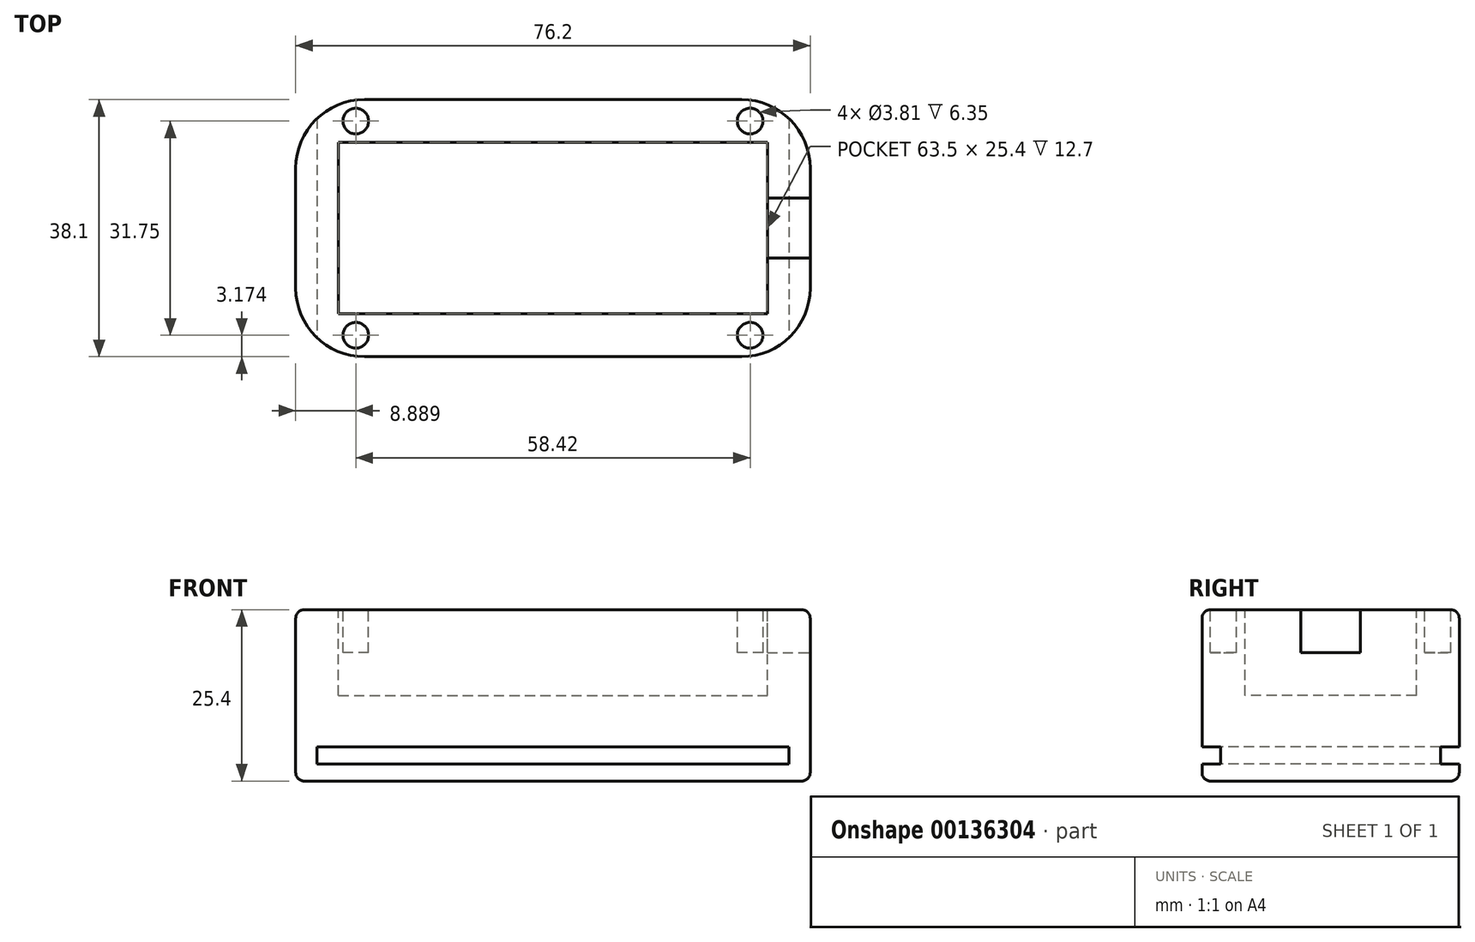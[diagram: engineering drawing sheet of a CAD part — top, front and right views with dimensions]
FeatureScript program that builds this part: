
annotation { "Feature Type Name" : "Feature", "Feature Type Description" : "" }
export const myFeature = defineFeature(function(context is Context, id is Id, definition is map)
    precondition{}
    {
        {
            var Q0;
            Q0=qCreatedBy(makeId("Top.planeOp"),FACE);
            var sketch = newSketch(context, id + "F0", { "sketchPlane" : qUnion([Q0])});
            skLineSegment(sketch, "E0.bottom", {"start": v(-49.17, 10.49) * mm, "end": v(27.03, 10.49) * mm});
            skLineSegment(sketch, "E0.top", {"start": v(-49.17, -27.61) * mm, "end": v(27.03, -27.61) * mm});
            skLineSegment(sketch, "E0.left", {"start": v(-49.17, 10.49) * mm, "end": v(-49.17, -27.61) * mm});
            skLineSegment(sketch, "E0.right", {"start": v(27.03, 10.49) * mm, "end": v(27.03, -27.61) * mm});
            skSolve(sketch);
        }
        {
            var Q0;
            Q0=makeQuery(id+"F0.imprint","IMPRINT",FACE,{"disambiguationData":[TD([[makeQuery(id+"F0.imprint","IMPRINT",EDGE,{"derivedFrom":sQuery(id+"F0.wireOp",EDGE,"E0.bottom")}),-1.0]])]});
            extrude(context, id + "F1", {"entities" : qUnion([Q0]), "depth" : 25.4 * mm});
        }
        {
            var Q0;
            Q0=makeQuery(id+"F1.opExtrude","SWEPT_FACE",FACE,{"disambiguationData":[OSD([sQuery(id+"F0.wireOp",EDGE,"E0.top")])]});
            var sketch = newSketch(context, id + "F2", { "sketchPlane" : qUnion([Q0])});
            skLineSegment(sketch, "E1.bottom", {"start": v(-46, 5.08) * mm, "end": v(23.85, 5.08) * mm});
            skLineSegment(sketch, "E1.top", {"start": v(-46, 2.54) * mm, "end": v(23.85, 2.54) * mm});
            skLineSegment(sketch, "E1.left", {"start": v(-46, 5.08) * mm, "end": v(-46, 2.54) * mm});
            skLineSegment(sketch, "E1.right", {"start": v(23.85, 5.08) * mm, "end": v(23.85, 2.54) * mm});
            skSolve(sketch);
        }
        {
            var Q0;
            Q0=makeQuery(id+"F2.imprint","IMPRINT",FACE,{"disambiguationData":[TD([[makeQuery(id+"F2.imprint","IMPRINT",EDGE,{"derivedFrom":sQuery(id+"F2.wireOp",EDGE,"E1.bottom")}),-1.0]])]});
            extrude(context, id + "F3", {"entities" : qUnion([Q0]), "operationType" : NewBodyOperationType.REMOVE, "endBound" : BoundingType.THROUGH_ALL, "oppositeDirection" : true, "depth" : 25.4 * mm});
        }
        {
            var Q0;
            Q0=makeQuery(id+"F1.opExtrude","CAP_FACE",FACE,{"disambiguationData":[OSD([sQuery(id+"F0.wireOp",EDGE,"E0.bottom"),sQuery(id+"F0.wireOp",EDGE,"E0.top"),sQuery(id+"F0.wireOp",EDGE,"E0.left"),sQuery(id+"F0.wireOp",EDGE,"E0.right")])],"isStart":false});
            var sketch = newSketch(context, id + "F4", { "sketchPlane" : qUnion([Q0])});
            skLineSegment(sketch, "E2.bottom", {"start": v(-42.82, 4.14) * mm, "end": v(20.68, 4.14) * mm});
            skLineSegment(sketch, "E2.top", {"start": v(-42.82, -21.26) * mm, "end": v(20.68, -21.26) * mm});
            skLineSegment(sketch, "E2.left", {"start": v(-42.82, 4.14) * mm, "end": v(-42.82, -21.26) * mm});
            skLineSegment(sketch, "E2.right", {"start": v(20.68, 4.14) * mm, "end": v(20.68, -21.26) * mm});
            skSolve(sketch);
        }
        {
            var Q0;
            Q0=makeQuery(id+"F4.imprint","IMPRINT",FACE,{"disambiguationData":[TD([[makeQuery(id+"F4.imprint","IMPRINT",EDGE,{"derivedFrom":sQuery(id+"F4.wireOp",EDGE,"E2.bottom")}),-1.0]])]});
            var Q1;
            Q1 = qSketchRegion(id + "F4", true);
            extrude(context, id + "F5", {"entities" : qUnion([Q0, Q1]), "operationType" : NewBodyOperationType.REMOVE, "oppositeDirection" : true, "depth" : 12.7 * mm});
        }
        {
            var Q0;
            Q0=makeQuery(id+"F1.opExtrude","CAP_FACE",FACE,{"disambiguationData":[OSD([sQuery(id+"F0.wireOp",EDGE,"E0.bottom"),sQuery(id+"F0.wireOp",EDGE,"E0.top"),sQuery(id+"F0.wireOp",EDGE,"E0.left"),sQuery(id+"F0.wireOp",EDGE,"E0.right")])],"isStart":false});
            var sketch = newSketch(context, id + "F6", { "sketchPlane" : qUnion([Q0])});
            skLineSegment(sketch, "E3.bottom", {"start": v(20.68, -4.12) * mm, "end": v(27.03, -4.12) * mm});
            skLineSegment(sketch, "E3.top", {"start": v(20.68, -13) * mm, "end": v(27.03, -13) * mm});
            skLineSegment(sketch, "E3.left", {"start": v(20.68, -4.12) * mm, "end": v(20.68, -13) * mm});
            skLineSegment(sketch, "E3.right", {"start": v(27.03, -4.12) * mm, "end": v(27.03, -13) * mm});
            skSolve(sketch);
        }
        {
            var Q0;
            Q0=makeQuery(id+"F6.imprint","IMPRINT",FACE,{"disambiguationData":[TD([[makeQuery(id+"F6.imprint","IMPRINT",EDGE,{"derivedFrom":sQuery(id+"F6.wireOp",EDGE,"E3.bottom")}),-1.0]])]});
            extrude(context, id + "F7", {"entities" : qUnion([Q0]), "operationType" : NewBodyOperationType.REMOVE, "oppositeDirection" : true, "depth" : 6.35 * mm});
        }
        {
            var Q0;
            Q0=makeQuery(id+"F1.opExtrude","CAP_FACE",FACE,{"disambiguationData":[OSD([sQuery(id+"F0.wireOp",EDGE,"E0.bottom"),sQuery(id+"F0.wireOp",EDGE,"E0.top"),sQuery(id+"F0.wireOp",EDGE,"E0.left"),sQuery(id+"F0.wireOp",EDGE,"E0.right")])],"isStart":false});
            var sketch = newSketch(context, id + "F8", { "sketchPlane" : qUnion([Q0])});
            skCircle(sketch, "E4", {"center": v(-40.28, 7.31) * mm, "radius": 1.9 * mm});
            skCircle(sketch, "E5", {"center": v(18.14, 7.31) * mm, "radius": 1.9 * mm});
            skCircle(sketch, "E6", {"center": v(-40.28, -24.44) * mm, "radius": 1.9 * mm});
            skCircle(sketch, "E7", {"center": v(18.14, -24.44) * mm, "radius": 1.9 * mm});
            skSolve(sketch);
        }
        {
            var Q0;
            Q0 = qSketchRegion(id + "F8", true);
            extrude(context, id + "F9", {"entities" : qUnion([Q0]), "operationType" : NewBodyOperationType.REMOVE, "oppositeDirection" : true, "depth" : 6.35 * mm});
        }
        {
            var Q0;
            Q0=makeQuery(id+"F1.opExtrude","SWEPT_EDGE",EDGE,{"disambiguationData":[OSD([sQuery(id+"F0.wireOp",EDGE,"E0.top"),sQuery(id+"F0.wireOp",EDGE,"E0.left")])]});
            var Q1;
            Q1=makeQuery(id+"F1.opExtrude","SWEPT_EDGE",EDGE,{"disambiguationData":[OSD([sQuery(id+"F0.wireOp",EDGE,"E0.top"),sQuery(id+"F0.wireOp",EDGE,"E0.right")])]});
            var Q2;
            Q2=makeQuery(id+"F1.opExtrude","SWEPT_EDGE",EDGE,{"disambiguationData":[OSD([sQuery(id+"F0.wireOp",EDGE,"E0.bottom"),sQuery(id+"F0.wireOp",EDGE,"E0.right")])]});
            var Q3;
            Q3=makeQuery(id+"F1.opExtrude","SWEPT_EDGE",EDGE,{"disambiguationData":[OSD([sQuery(id+"F0.wireOp",EDGE,"E0.bottom"),sQuery(id+"F0.wireOp",EDGE,"E0.left")])]});
            fillet(context, id + "F10", {"entities" : qUnion([Q0, Q1, Q2, Q3]), "radius" : 10.16 * mm, "tangentPropagation" : true, "allowEdgeOverflow" : false});
        }
        {
            var Q0;
            Q0=makeQuery(id+"F1.opExtrude","CAP_EDGE",EDGE,{"disambiguationData":[OSD([sQuery(id+"F0.wireOp",EDGE,"E0.left")])],"isStart":false});
            var Q1;
            Q1=makeQuery(id+"F1.opExtrude","CAP_EDGE",EDGE,{"disambiguationData":[OSD([sQuery(id+"F0.wireOp",EDGE,"E0.bottom")])],"isStart":true});
            var Q2;
            Q2=makeQuery(id+"F1.opExtrude","CAP_EDGE",EDGE,{"disambiguationData":[OSD([sQuery(id+"F0.wireOp",EDGE,"E0.top")])],"isStart":true});
            var Q3;
            Q3=makeQuery(id+"F1.opExtrude","CAP_EDGE",EDGE,{"disambiguationData":[OSD([sQuery(id+"F0.wireOp",EDGE,"E0.right")])],"isStart":true});
            var Q4;
            Q4=makeQuery(id+"F1.opExtrude","CAP_EDGE",EDGE,{"disambiguationData":[OSD([sQuery(id+"F0.wireOp",EDGE,"E0.left")])],"isStart":true});
            fillet(context, id + "F11", {"entities" : qUnion([Q0, Q1, Q2, Q3, Q4]), "radius" : 1.27 * mm, "tangentPropagation" : true, "allowEdgeOverflow" : false});
        }
    });
